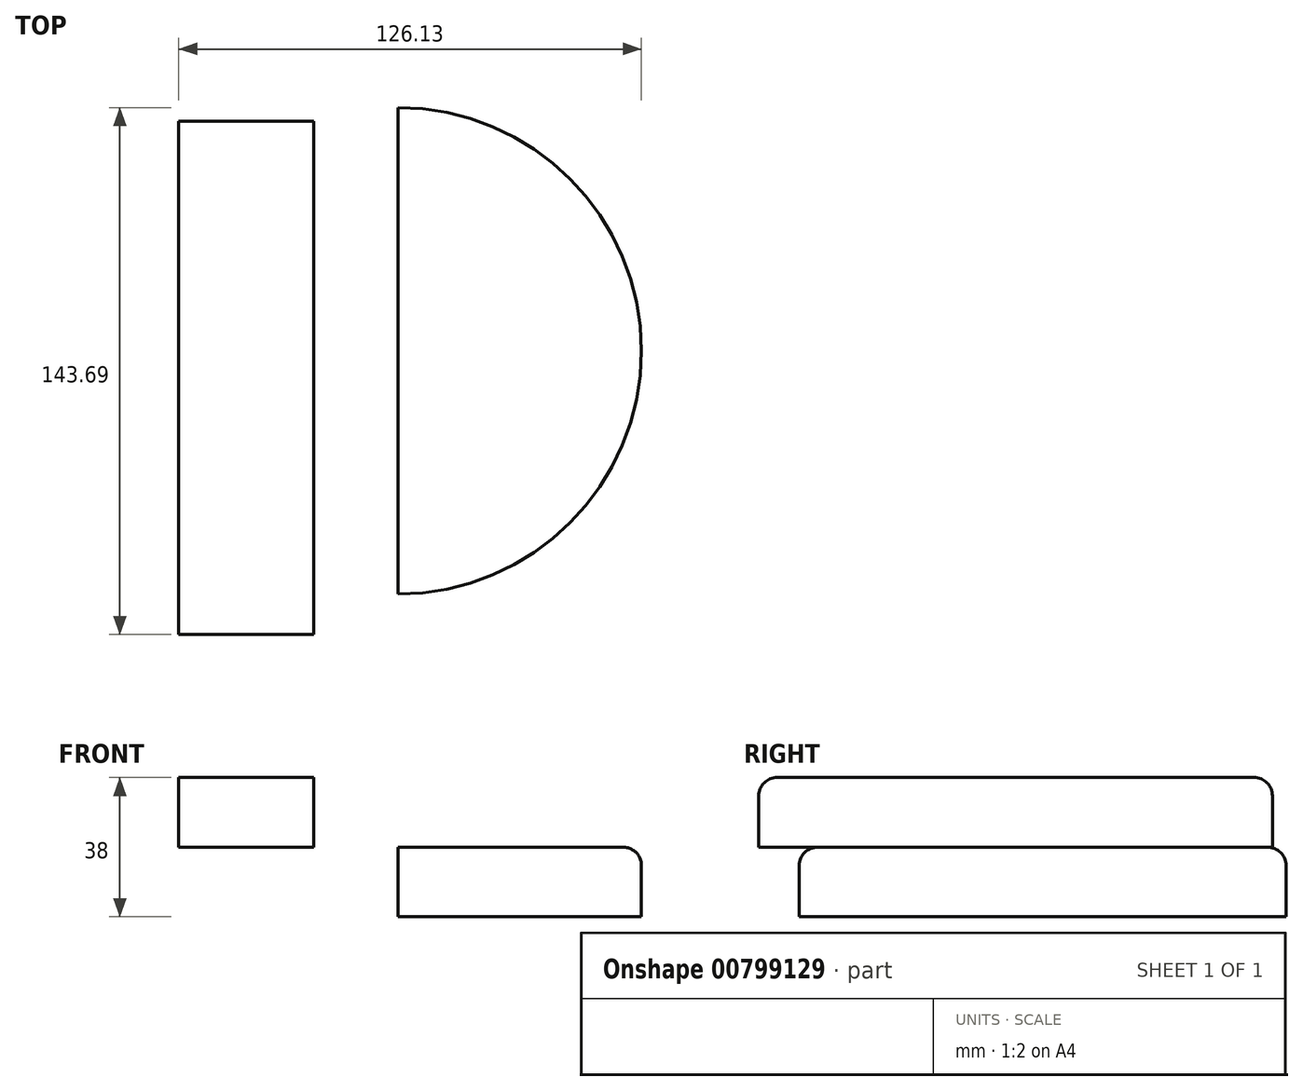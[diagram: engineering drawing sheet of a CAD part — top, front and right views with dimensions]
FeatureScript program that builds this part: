
annotation { "Feature Type Name" : "Feature", "Feature Type Description" : "" }
export const myFeature = defineFeature(function(context is Context, id is Id, definition is map)
    precondition{}
    {
        {
            var Q0;
            Q0=qCreatedBy(makeId("Top.planeOp"),FACE);
            var sketch = newSketch(context, id + "F0", { "sketchPlane" : qUnion([Q0])});
            skLineSegment(sketch, "E0", {"start": v(0, -66.33) * mm, "end": v(0, 66.33) * mm});
            skArc(sketch, "E1", {"start": v(0, 66.33) * mm, "mid": v(-66.33, 0) * mm, "end": v(0, -66.33) * mm});
            skArc(sketch, "E2", {"start": v(0, -66.33) * mm, "mid": v(66.33, 0) * mm, "end": v(0, 66.33) * mm});
            skSolve(sketch);
        }
        {
            var Q0;
            Q0=makeQuery(id+"F0.imprint","IMPRINT",FACE,{"disambiguationData":[TD([[makeQuery(id+"F0.imprint","IMPRINT",EDGE,{"derivedFrom":sQuery(id+"F0.wireOp",EDGE,"E0")}),-1.0]])]});
            extrude(context, id + "F1", {"entities" : qUnion([Q0]), "depth" : 19 * mm, "offsetDistance" : 25 * mm});
        }
        {
            var Q0;
            Q0=makeQuery(id+"F1.opExtrude","CAP_FACE",FACE,{"disambiguationData":[OSD([sQuery(id+"F0.wireOp",EDGE,"E0"),sQuery(id+"F0.wireOp",EDGE,"E2")])],"isStart":false});
            var sketch = newSketch(context, id + "F2", { "sketchPlane" : qUnion([Q0])});
            skLineSegment(sketch, "E3.bottom", {"start": v(-23.04, -77.36) * mm, "end": v(-59.8, -77.36) * mm});
            skLineSegment(sketch, "E3.top", {"start": v(-23.04, 62.64) * mm, "end": v(-59.8, 62.64) * mm});
            skLineSegment(sketch, "E3.left", {"start": v(-23.04, -77.36) * mm, "end": v(-23.04, 62.64) * mm});
            skLineSegment(sketch, "E3.right", {"start": v(-59.8, -77.36) * mm, "end": v(-59.8, 62.64) * mm});
            skSolve(sketch);
        }
        {
            var Q0;
            Q0=makeQuery(id+"F2.imprint","IMPRINT",FACE,{"disambiguationData":[TD([[makeQuery(id+"F2.imprint","IMPRINT",EDGE,{"derivedFrom":sQuery(id+"F2.wireOp",EDGE,"E3.bottom")}),-1.0]])]});
            extrude(context, id + "F3", {"entities" : qUnion([Q0]), "depth" : 19 * mm, "offsetDistance" : 25 * mm});
        }
        {
            var Q0;
            Q0=makeQuery(id+"F1.opExtrude","CAP_EDGE",EDGE,{"disambiguationData":[OSD([sQuery(id+"F0.wireOp",EDGE,"E2")])],"isStart":false});
            fillet(context, id + "F4", {"entities" : qUnion([Q0]), "radius" : 5 * mm, "tangentPropagation" : true, "allowEdgeOverflow" : false});
        }
        {
            var Q0;
            Q0=makeQuery(id+"F3.opExtrude","CAP_EDGE",EDGE,{"disambiguationData":[OSD([sQuery(id+"F2.wireOp",EDGE,"E3.bottom")])],"isStart":false});
            var Q1;
            Q1=makeQuery(id+"F3.opExtrude","CAP_EDGE",EDGE,{"disambiguationData":[OSD([sQuery(id+"F2.wireOp",EDGE,"E3.top")])],"isStart":false});
            fillet(context, id + "F5", {"entities" : qUnion([Q0, Q1]), "radius" : 5 * mm, "tangentPropagation" : true, "allowEdgeOverflow" : false});
        }
    });
